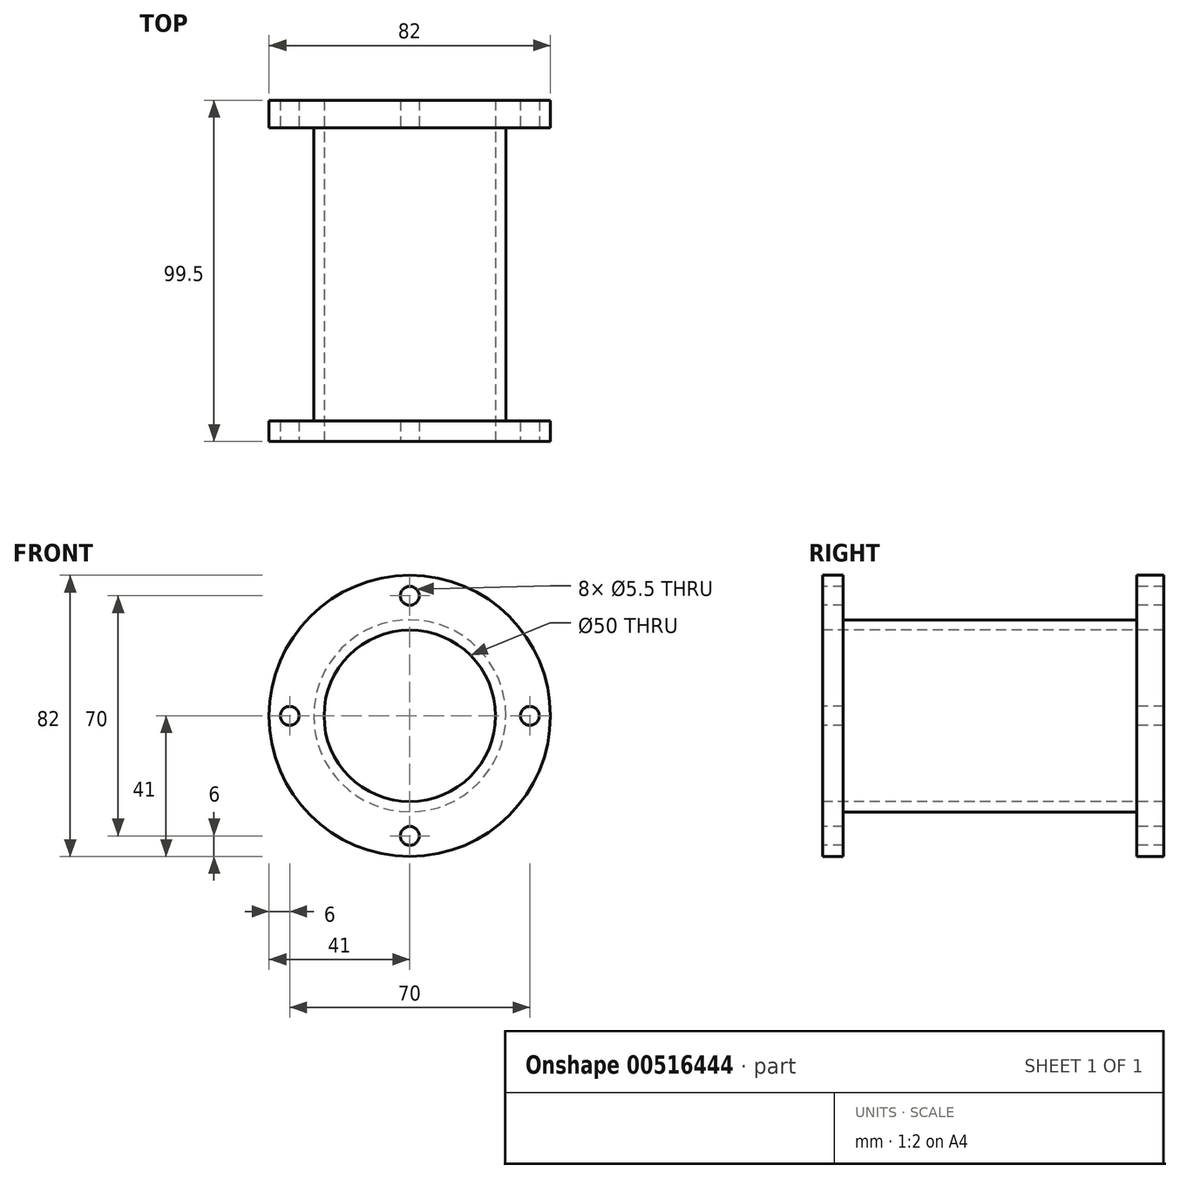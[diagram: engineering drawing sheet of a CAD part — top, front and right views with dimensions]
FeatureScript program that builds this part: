
annotation { "Feature Type Name" : "Feature", "Feature Type Description" : "" }
export const myFeature = defineFeature(function(context is Context, id is Id, definition is map)
    precondition{}
    {
        {
            var Q0;
            Q0=qCreatedBy(makeId("Front.planeOp"),FACE);
            var sketch = newSketch(context, id + "F0", { "sketchPlane" : qUnion([Q0])});
            skCircle(sketch, "E0", {"center": v(0, 0) * mm, "radius": 41 * mm});
            skSolve(sketch);
        }
        {
            var Q0;
            Q0=makeQuery(id+"F0.imprint","IMPRINT",FACE,{"disambiguationData":[TD([[makeQuery(id+"F0.imprint","IMPRINT",EDGE,{"derivedFrom":sQuery(id+"F0.wireOp",EDGE,"E0")}),1.0]])]});
            extrude(context, id + "F1", {"entities" : qUnion([Q0]), "depth" : 8 * mm, "offsetDistance" : 25 * mm});
        }
        {
            var Q0;
            Q0=makeQuery(id+"F1.opExtrude","CAP_FACE",FACE,{"disambiguationData":[OSD([sQuery(id+"F0.wireOp",EDGE,"E0")])],"isStart":false});
            var sketch = newSketch(context, id + "F2", { "sketchPlane" : qUnion([Q0])});
            skCircle(sketch, "E1", {"center": v(0, 0) * mm, "radius": 28 * mm});
            skSolve(sketch);
        }
        {
            var Q0;
            Q0=makeQuery(id+"F2.imprint","IMPRINT",FACE,{"disambiguationData":[TD([[makeQuery(id+"F2.imprint","IMPRINT",EDGE,{"derivedFrom":sQuery(id+"F2.wireOp",EDGE,"E1")}),1.0]])]});
            extrude(context, id + "F3", {"entities" : qUnion([Q0]), "operationType" : NewBodyOperationType.ADD, "depth" : 85.5 * mm, "offsetDistance" : 25 * mm});
        }
        {
            var Q0;
            Q0=makeQuery(id+"F3.opExtrude","CAP_FACE",FACE,{"disambiguationData":[OSD([sQuery(id+"F2.wireOp",EDGE,"E1")])],"isStart":false});
            var sketch = newSketch(context, id + "F4", { "sketchPlane" : qUnion([Q0])});
            skCircle(sketch, "E2", {"center": v(0, 0) * mm, "radius": 41 * mm});
            skSolve(sketch);
        }
        {
            var Q0;
            Q0=makeQuery(id+"F4.imprint","IMPRINT",FACE,{"disambiguationData":[TD([[makeQuery(id+"F4.imprint","IMPRINT",EDGE,{"derivedFrom":makeQuery(id+"F3.opExtrude","CAP_EDGE",EDGE,{"disambiguationData":[OSD([sQuery(id+"F2.wireOp",EDGE,"E1")])],"isStart":false})}),1.0]])]});
            var Q1;
            Q1=makeQuery(id+"F4.imprint","IMPRINT",FACE,{"disambiguationData":[TD([[makeQuery(id+"F4.imprint","IMPRINT",EDGE,{"derivedFrom":sQuery(id+"F4.wireOp",EDGE,"E2")}),1.0]])]});
            extrude(context, id + "F5", {"entities" : qUnion([Q0, Q1]), "operationType" : NewBodyOperationType.ADD, "depth" : 6 * mm, "offsetDistance" : 25 * mm});
        }
        {
            var Q0;
            Q0=makeQuery(id+"F5.opExtrude","CAP_FACE",FACE,{"disambiguationData":[OSD([sQuery(id+"F4.wireOp",EDGE,"E2")])],"isStart":false});
            var sketch = newSketch(context, id + "F6", { "sketchPlane" : qUnion([Q0])});
            skCircle(sketch, "E3", {"center": v(0, 0) * mm, "radius": 25 * mm});
            skSolve(sketch);
        }
        {
            var Q0;
            Q0=makeQuery(id+"F6.imprint","IMPRINT",FACE,{"disambiguationData":[TD([[makeQuery(id+"F6.imprint","IMPRINT",EDGE,{"derivedFrom":sQuery(id+"F6.wireOp",EDGE,"E3")}),1.0]])]});
            extrude(context, id + "F7", {"entities" : qUnion([Q0]), "operationType" : NewBodyOperationType.REMOVE, "endBound" : BoundingType.THROUGH_ALL, "oppositeDirection" : true, "depth" : 25 * mm, "offsetDistance" : 25 * mm});
        }
        {
            var Q0;
            Q0=makeQuery(id+"F5.opExtrude","CAP_FACE",FACE,{"disambiguationData":[OSD([sQuery(id+"F4.wireOp",EDGE,"E2")])],"isStart":false});
            var sketch = newSketch(context, id + "F8", { "sketchPlane" : qUnion([Q0])});
            skCircle(sketch, "E4", {"center": v(0, 35) * mm, "radius": 2.75 * mm});
            skCircle(sketch, "E5", {"center": v(0, 0) * mm, "radius": 35 * mm, "construction": true});
            skLineSegment(sketch, "E6", {"start": v(0, 0) * mm, "end": v(0, 35) * mm, "construction": true});
            skCircle(sketch, "E7.1.0", {"center": v(-35, 0) * mm, "radius": 2.75 * mm});
            skCircle(sketch, "E7.2.0", {"center": v(0, -35) * mm, "radius": 2.75 * mm});
            skCircle(sketch, "E7.3.0", {"center": v(35, 0) * mm, "radius": 2.75 * mm});
            skSolve(sketch);
        }
        {
            var Q0;
            Q0=makeQuery(id+"F8.imprint","IMPRINT",FACE,{"disambiguationData":[TD([[makeQuery(id+"F8.imprint","IMPRINT",EDGE,{"derivedFrom":sQuery(id+"F8.wireOp",EDGE,"E7.1.0")}),1.0]])]});
            var Q1;
            Q1=makeQuery(id+"F8.imprint","IMPRINT",FACE,{"disambiguationData":[TD([[makeQuery(id+"F8.imprint","IMPRINT",EDGE,{"derivedFrom":sQuery(id+"F8.wireOp",EDGE,"E4")}),1.0]])]});
            var Q2;
            Q2=makeQuery(id+"F8.imprint","IMPRINT",FACE,{"disambiguationData":[TD([[makeQuery(id+"F8.imprint","IMPRINT",EDGE,{"derivedFrom":sQuery(id+"F8.wireOp",EDGE,"E7.3.0")}),1.0]])]});
            var Q3;
            Q3=makeQuery(id+"F8.imprint","IMPRINT",FACE,{"disambiguationData":[TD([[makeQuery(id+"F8.imprint","IMPRINT",EDGE,{"derivedFrom":sQuery(id+"F8.wireOp",EDGE,"E7.2.0")}),1.0]])]});
            extrude(context, id + "F9", {"entities" : qUnion([Q0, Q1, Q2, Q3]), "operationType" : NewBodyOperationType.REMOVE, "endBound" : BoundingType.THROUGH_ALL, "oppositeDirection" : true, "depth" : 25 * mm, "offsetDistance" : 25 * mm});
        }
    });
